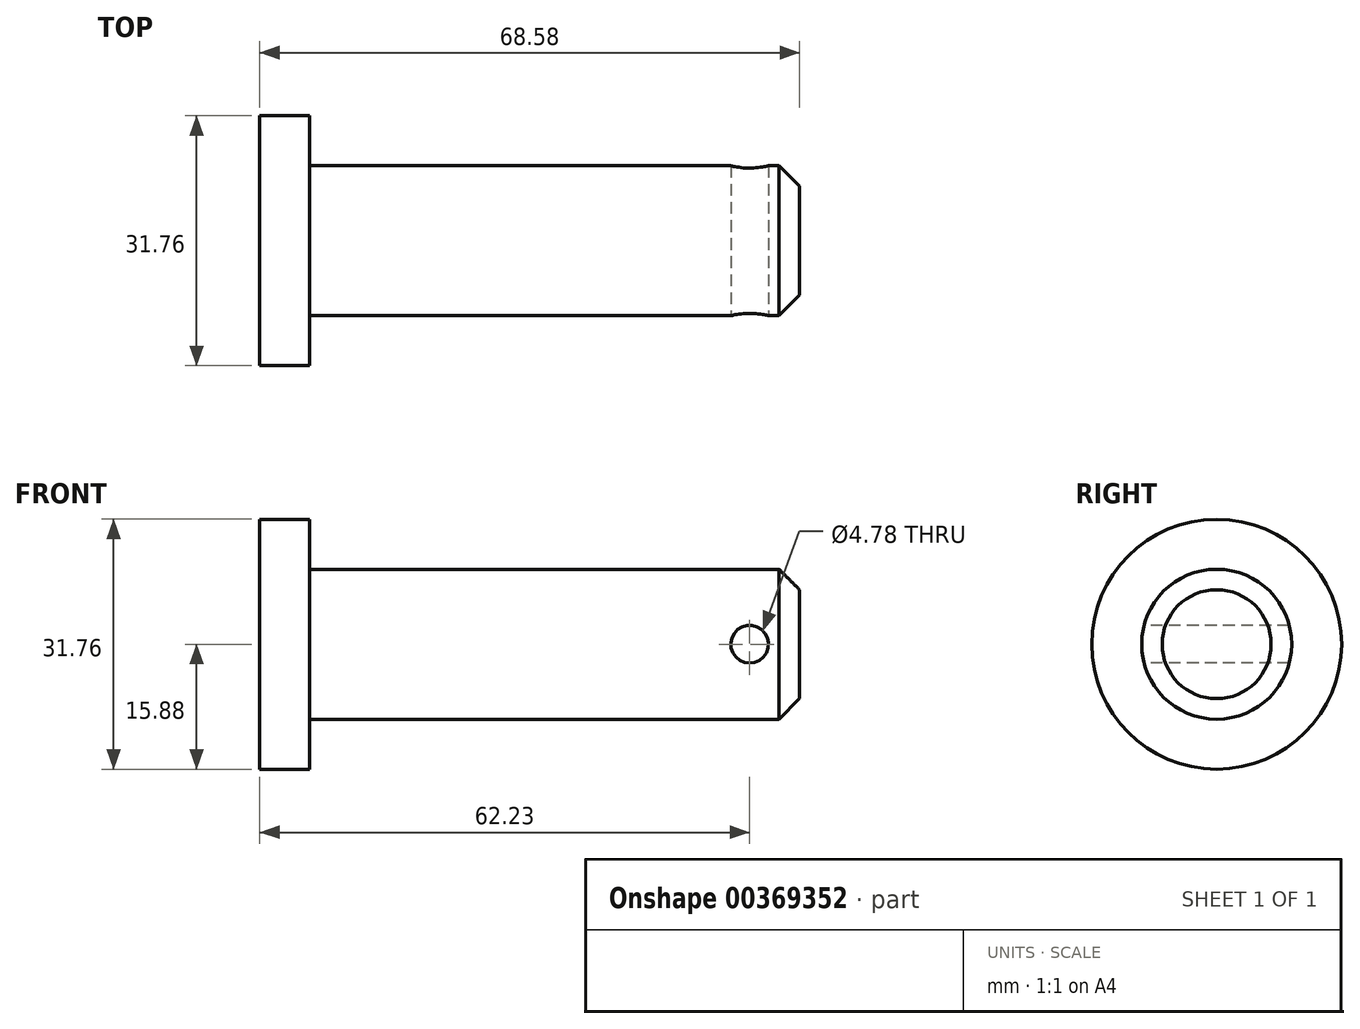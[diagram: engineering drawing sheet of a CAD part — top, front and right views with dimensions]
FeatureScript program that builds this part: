
annotation { "Feature Type Name" : "Feature", "Feature Type Description" : "" }
export const myFeature = defineFeature(function(context is Context, id is Id, definition is map)
    precondition{}
    {
        {
            var Q0;
            Q0=qCreatedBy(makeId("Front.planeOp"),FACE);
            var sketch = newSketch(context, id + "F0", { "sketchPlane" : qUnion([Q0])});
            skLineSegment(sketch, "E0", {"start": v(-28.3, 0) * mm, "end": v(83.24, 0) * mm, "construction": true});
            skLineSegment(sketch, "E1", {"start": v(0, 0) * mm, "end": v(0, 15.88) * mm});
            skLineSegment(sketch, "E2", {"start": v(0, 15.88) * mm, "end": v(6.35, 15.88) * mm});
            skLineSegment(sketch, "E3", {"start": v(6.35, 15.88) * mm, "end": v(6.35, 0) * mm});
            skLineSegment(sketch, "E4", {"start": v(6.35, 0) * mm, "end": v(0, 0) * mm});
            skLineSegment(sketch, "E5", {"start": v(6.35, 9.53) * mm, "end": v(43.07, 9.53) * mm});
            skLineSegment(sketch, "E6", {"start": v(68.58, 6.92) * mm, "end": v(68.58, 0) * mm});
            skLineSegment(sketch, "E7", {"start": v(43.07, 9.53) * mm, "end": v(65.97, 9.53) * mm});
            skLineSegment(sketch, "E8", {"start": v(65.97, 9.53) * mm, "end": v(68.58, 6.92) * mm});
            skPoint(sketch, "E9", {"position": v(65.97, 9.53) * mm});
            skPoint(sketch, "E10", {"position": v(68.58, 6.92) * mm});
            skPoint(sketch, "E11.start.orphan", {"position": v(43.07, 0) * mm});
            skLineSegment(sketch, "E12", {"start": v(6.35, 0) * mm, "end": v(68.58, 0) * mm});
            skLineSegment(sketch, "E13", {"start": v(65.97, 9.53) * mm, "end": v(65.97, 0) * mm});
            skCircle(sketch, "E14", {"center": v(62.23, 0) * mm, "radius": 2.39 * mm});
            skSolve(sketch);
        }
        {
            var Q0;
            {var subQ5=sQuery(id+"F0.wireOp",EDGE,"E5");Q0=makeQuery(id+"F0.imprint","IMPRINT",FACE,{"disambiguationData":[TD([[makeQuery(id+"F0.imprint","IMPRINT",EDGE,{"derivedFrom":subQ5}),-1.0]])]});}
            var Q1;
            Q1=makeQuery(id+"F0.imprint","IMPRINT",FACE,{"disambiguationData":[TD([[makeQuery(id+"F0.imprint","IMPRINT",EDGE,{"derivedFrom":sQuery(id+"F0.wireOp",EDGE,"E1")}),-1.0]])]});
            var Q2;
            {var subQ0=sQuery(id+"F0.wireOp",EDGE,"E6");Q2=makeQuery(id+"F0.imprint","IMPRINT",FACE,{"disambiguationData":[TD([[makeQuery(id+"F0.imprint","IMPRINT",EDGE,{"derivedFrom":subQ0}),-1.0]])]});}
            var Q3;
            Q3=sQuery(id+"F0.wireOp",EDGE,"E0");
            revolve(context, id + "F1", {"entities" : qUnion([Q0, Q1, Q2]), "axis" : qUnion([Q3]), "revolveType" : RevolveType.FULL});
        }
        {
            var Q0;
            {var subQ0=sQuery(id+"F0.wireOp",EDGE,"E14");var subQ1=sQuery(id+"F0.wireOp",EDGE,"E12");var subQ2=makeQuery(id+"F0.imprint","INTERSECT",VERTEX,{"disambiguationData":[OD(0.0)],"derivedFrom":[subQ1,subQ0]});Q0=makeQuery(id+"F0.imprint","IMPRINT",FACE,{"disambiguationData":[TD([[makeQuery(id+"F0.imprint","IMPRINT",EDGE,{"disambiguationData":[TD([[subQ2,-1.0]])],"derivedFrom":subQ1}),1.0]])]});}
            var Q1;
            {var subQ0=sQuery(id+"F0.wireOp",EDGE,"E14");var subQ1=sQuery(id+"F0.wireOp",EDGE,"E12");var subQ2=makeQuery(id+"F0.imprint","INTERSECT",VERTEX,{"disambiguationData":[OD(0.0)],"derivedFrom":[subQ1,subQ0]});Q1=makeQuery(id+"F0.imprint","IMPRINT",FACE,{"disambiguationData":[TD([[makeQuery(id+"F0.imprint","IMPRINT",EDGE,{"disambiguationData":[TD([[subQ2,-1.0]])],"derivedFrom":subQ1}),-1.0]])]});}
            var Q2;
            Q2=sQuery(id+"F0.wireOp",EDGE,"E14");
            extrude(context, id + "F2", {"entities" : qUnion([Q0, Q1]), "operationType" : NewBodyOperationType.REMOVE, "surfaceEntities" : qUnion([Q2]), "endBound" : BoundingType.SYMMETRIC, "oppositeDirection" : true, "depth" : 25.4 * mm});
        }
    });
